# Revit family: Sanitary_Showers_AXOR_39748XXX-AXOR-Citterio-Next-Overhead-shower-370-1jet-shower-arm
name_source: partatom
category: Plumbing Fixtures
units: mm (PartAtom-declared; Revit-internal decimal feet)

## family parameters
Always vertical = No
Cut with Voids When Loaded = No
Maintain Annotation Orientation = No
OmniClass Number = 23.31.17.19
OmniClass Title = Shower Head Fixtures
Part Type = Normal
Room Calculation Point = No
Round Connector Dimension = Use Diameter
Shared = No
Work Plane-Based = Yes

## types (1)
- 000 Chrome
    CW Connection = No
    CWFU = 0
    Connector Description = Water Inlet 12.7mm
    Cost = 0 $
    Default Elevation = 0 mm  [stored 0 ft]
    Description = 39748XXX AXOR Citterio Next Overhead shower 370 1jet with shower arm
    Diameter = 13 mm
    HW Connection = No
    HWFU = 0
    Manufacturer = AXOR
    Material 1 = Hansgrohe - Metal - 000 Chrome
    Model = 39748XXX
    Product Page URL = https://www.axor-design.com
    Product data url = https://bimobject.com
    URL = https://www.axor-design.com
    Vent Connection = No
    Version = 1
    WFU = 0
    Waste Connection = No

note: [stored X ft] marks values corroborated as IEEE doubles in the binary element streams (Revit-internal decimal feet)

## geometry (parser evidence)
native form markers: Sweep x3
no freeform markers — native parametric forms only
